# Revit family: Basin-SloanStone-Sloan-DSCT-82000
name_source: partatom
category: Plumbing Fixtures
revit_build: Autodesk Revit 2015 (Build: 20140606_1530(x64)
units: mm (PartAtom-declared; Revit-internal decimal feet)

## types (1)
- DSCT-82000
    ADA Compliant = Yes
    Assembly Code = D2010300
    Buy American Act Compliant = Yes
    CW Connection = Yes
    CWFU = 1.5
    Cold Water Connection Radius = 3/16"
    Default Elevation = 34"
    Description = Counter Top Basin Two Station Lavatory System can be equipped with Sloan® OPTIMA® SensorActivated Electronics. Constructed of durable Corian or natural stone, Both materials are available with our 20% or more post consumer recycled content.
    HW Connection = Yes
    HWFU = 1.5
    Hot Water Connection Radius = 3/16"
    Manufacturer = Sloan
    Material = SloanStone-Sloan-Designer White
    Model = DSCT-82000
    Product URL = http://www.sloanvalve.com
    Product data url = https://bimobject.com
    Revised Date = 11/13/15
    Specification Sheet = http://www.sloanvalve.com
    URL = http://www.sloanvalve.com
    Vent Connection = No
    WFU = 2
    Warranty = 3 year (limited)
    Waste Connection = Yes
    Waste Connection Radius = 5/8"

## geometry (parser evidence)
native form markers: Sweep x1
no freeform markers — native parametric forms only
